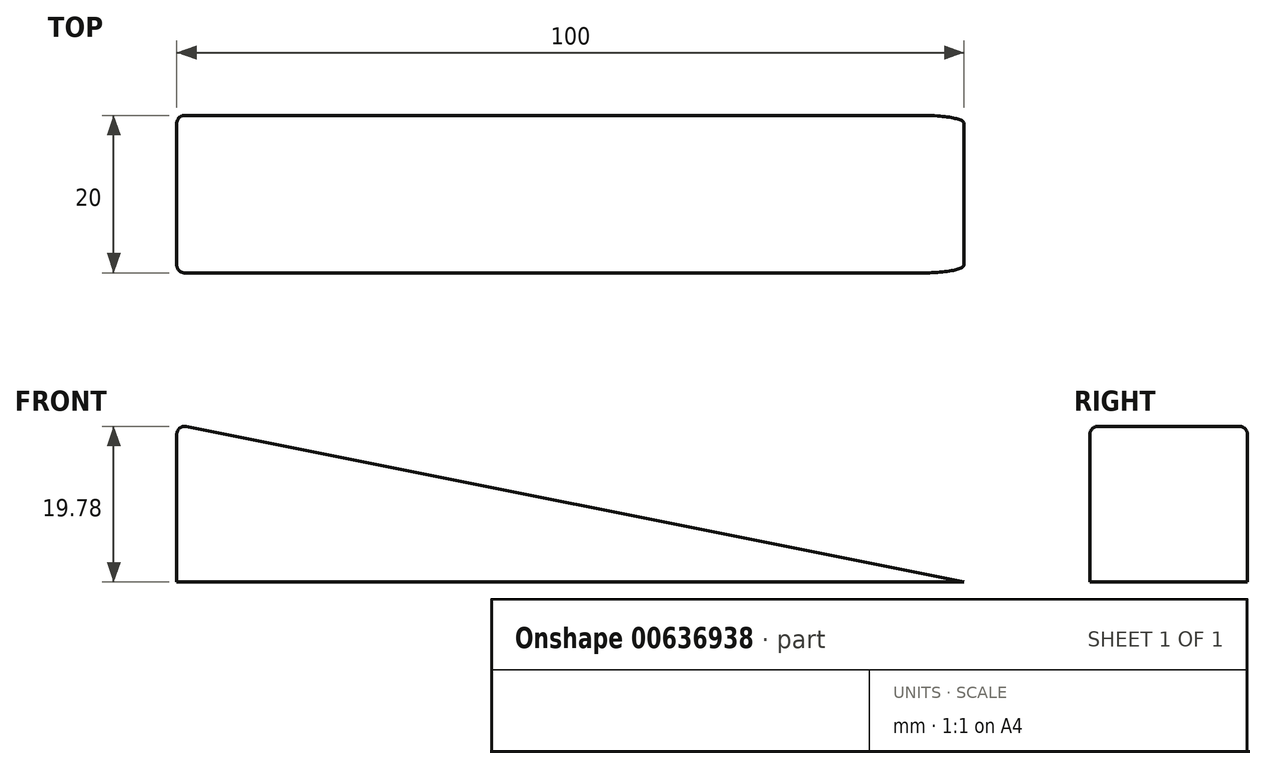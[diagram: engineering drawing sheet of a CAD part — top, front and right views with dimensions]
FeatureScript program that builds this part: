
annotation { "Feature Type Name" : "Feature", "Feature Type Description" : "" }
export const myFeature = defineFeature(function(context is Context, id is Id, definition is map)
    precondition{}
    {
        {
            var Q0;
            Q0=qCreatedBy(makeId("Front.planeOp"),FACE);
            var sketch = newSketch(context, id + "F0", { "sketchPlane" : qUnion([Q0])});
            skLineSegment(sketch, "E0", {"start": v(0, 0) * mm, "end": v(100, 0) * mm});
            skLineSegment(sketch, "E1", {"start": v(100, 0) * mm, "end": v(0, 20) * mm});
            skLineSegment(sketch, "E2", {"start": v(0, 20) * mm, "end": v(0, 0) * mm});
            skSolve(sketch);
        }
        {
            var Q0;
            Q0 = qSketchRegion(id + "F0", true);
            extrude(context, id + "F1", {"entities" : qUnion([Q0]), "endBound" : BoundingType.SYMMETRIC, "depth" : 20 * mm, "offsetDistance" : 25 * mm});
        }
        {
            var Q0;
            Q0=makeQuery(id+"F1.opExtrude","CAP_EDGE",EDGE,{"disambiguationData":[OSD([sQuery(id+"F0.wireOp",EDGE,"E1")])],"isStart":false});
            var Q1;
            Q1=makeQuery(id+"F1.opExtrude","CAP_EDGE",EDGE,{"disambiguationData":[OSD([sQuery(id+"F0.wireOp",EDGE,"E1")])],"isStart":true});
            var Q2;
            Q2=makeQuery(id+"F1.opExtrude","SWEPT_EDGE",EDGE,{"disambiguationData":[OSD([sQuery(id+"F0.wireOp",EDGE,"E1"),sQuery(id+"F0.wireOp",EDGE,"E2")])]});
            var Q3;
            Q3=makeQuery(id+"F1.opExtrude","CAP_EDGE",EDGE,{"disambiguationData":[OSD([sQuery(id+"F0.wireOp",EDGE,"E2")])],"isStart":false});
            var Q4;
            Q4=makeQuery(id+"F1.opExtrude","CAP_EDGE",EDGE,{"disambiguationData":[OSD([sQuery(id+"F0.wireOp",EDGE,"E2")])],"isStart":true});
            fillet(context, id + "F2", {"entities" : qUnion([Q0, Q1, Q2, Q3, Q4]), "radius" : 1 * mm, "tangentPropagation" : true, "allowEdgeOverflow" : false});
        }
    });
